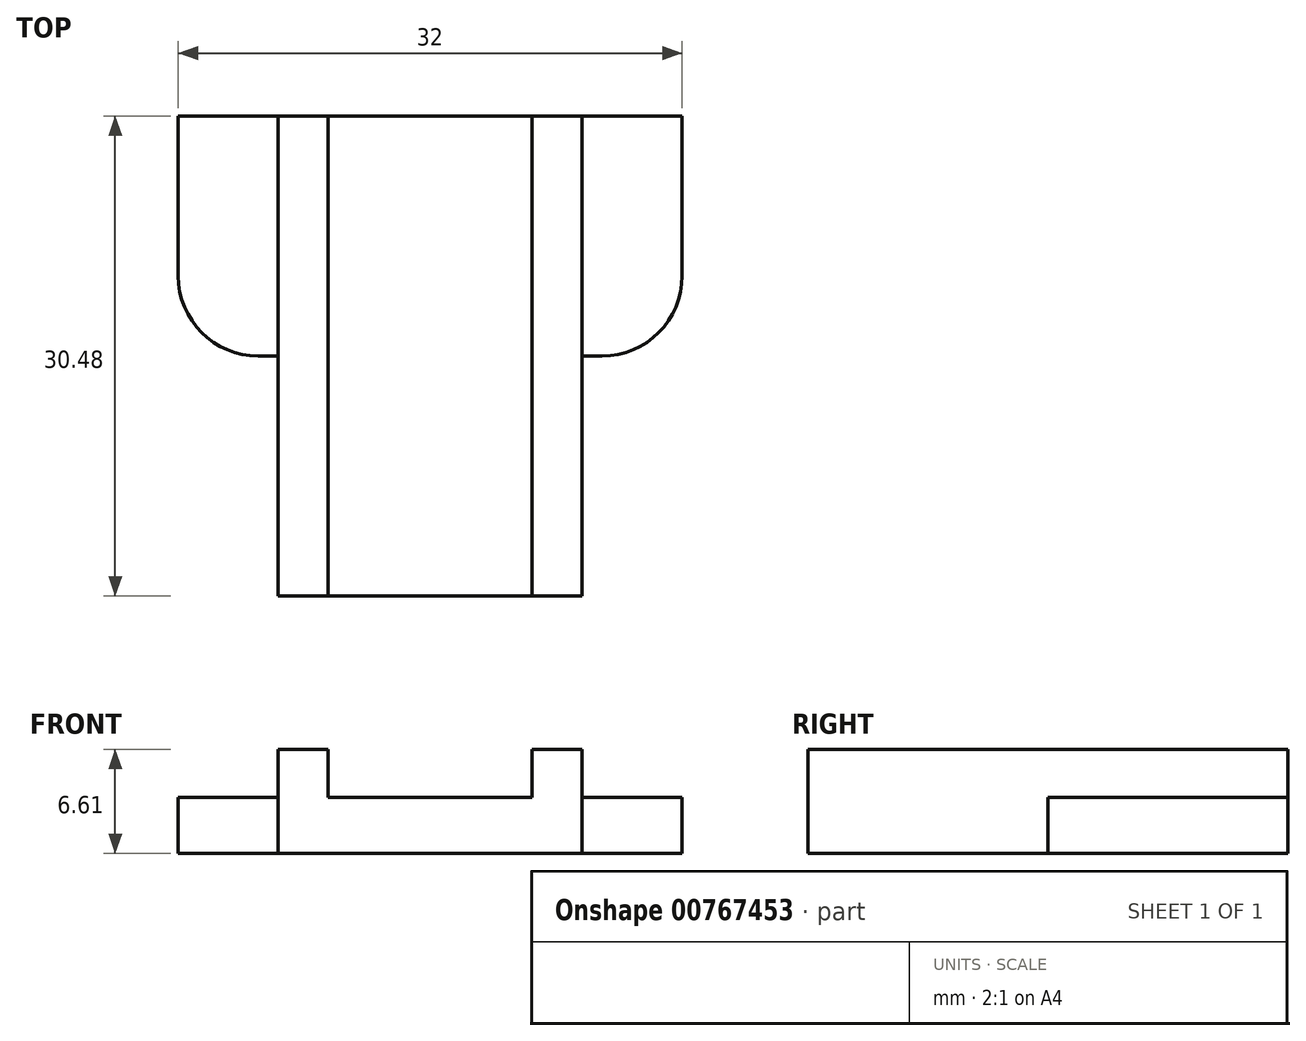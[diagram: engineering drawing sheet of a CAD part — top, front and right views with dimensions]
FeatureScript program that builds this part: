
annotation { "Feature Type Name" : "Feature", "Feature Type Description" : "" }
export const myFeature = defineFeature(function(context is Context, id is Id, definition is map)
    precondition{}
    {
        {
            var Q0;
            Q0=qCreatedBy(makeId("Front.planeOp"),FACE);
            var sketch = newSketch(context, id + "F0", { "sketchPlane" : qUnion([Q0])});
            skLineSegment(sketch, "E0.bottom", {"start": v(9.65, 1.78) * mm, "end": v(-9.65, 1.78) * mm});
            skLineSegment(sketch, "E0.top", {"start": v(9.65, -1.78) * mm, "end": v(-9.65, -1.78) * mm});
            skLineSegment(sketch, "E0.left", {"start": v(9.65, 1.78) * mm, "end": v(9.65, -1.78) * mm});
            skLineSegment(sketch, "E0.right", {"start": v(-9.65, 1.78) * mm, "end": v(-9.65, -1.78) * mm});
            skPoint(sketch, "E0.middle", {"position": v(0, 0) * mm});
            skLineSegment(sketch, "E1.bottom", {"start": v(9.65, 1.78) * mm, "end": v(6.48, 1.78) * mm});
            skLineSegment(sketch, "E1.top", {"start": v(9.65, 4.83) * mm, "end": v(6.48, 4.83) * mm});
            skLineSegment(sketch, "E1.left", {"start": v(9.65, 1.78) * mm, "end": v(9.65, 4.83) * mm});
            skLineSegment(sketch, "E1.right", {"start": v(6.48, 1.78) * mm, "end": v(6.48, 4.83) * mm});
            skPoint(sketch, "E1.middle", {"position": v(8.06, 3.3) * mm});
            skLineSegment(sketch, "E2.MirrorCS", {"start": v(-9.65, 1.78) * mm, "end": v(-6.48, 1.78) * mm});
            skLineSegment(sketch, "E3.MirrorCS", {"start": v(-6.48, 1.78) * mm, "end": v(-6.48, 4.83) * mm});
            skLineSegment(sketch, "E4.MirrorCS", {"start": v(-9.65, 4.83) * mm, "end": v(-6.48, 4.83) * mm});
            skLineSegment(sketch, "E5.MirrorCS", {"start": v(-9.65, 1.78) * mm, "end": v(-9.65, 4.83) * mm});
            skPoint(sketch, "E6.MirrorP", {"position": v(-8.06, 3.3) * mm});
            skLineSegment(sketch, "E7.bottom", {"start": v(6.48, 1.78) * mm, "end": v(-6.48, 1.78) * mm});
            skLineSegment(sketch, "E7.top", {"start": v(6.48, 4.83) * mm, "end": v(-6.48, 4.83) * mm});
            skLineSegment(sketch, "E8.bottom", {"start": v(9.65, 1.78) * mm, "end": v(16, 1.78) * mm});
            skLineSegment(sketch, "E8.top", {"start": v(9.65, -1.78) * mm, "end": v(16, -1.78) * mm});
            skLineSegment(sketch, "E8.right", {"start": v(16, 1.78) * mm, "end": v(16, -1.78) * mm});
            skLineSegment(sketch, "E9.MirrorCS", {"start": v(-9.65, -1.78) * mm, "end": v(-16, -1.78) * mm});
            skLineSegment(sketch, "E10.MirrorCS", {"start": v(-9.65, 1.78) * mm, "end": v(-16, 1.78) * mm});
            skLineSegment(sketch, "E11.MirrorCS", {"start": v(-16, 1.78) * mm, "end": v(-16, -1.78) * mm});
            skSolve(sketch);
        }
        {
            var Q0;
            Q0=makeQuery(id+"F0.imprint","IMPRINT",FACE,{"disambiguationData":[TD([[makeQuery(id+"F0.imprint","IMPRINT",EDGE,{"derivedFrom":sQuery(id+"F0.wireOp",EDGE,"E0.top")}),-1.0]])]});
            var Q1;
            Q1=makeQuery(id+"F0.imprint","IMPRINT",FACE,{"disambiguationData":[TD([[makeQuery(id+"F0.imprint","IMPRINT",EDGE,{"derivedFrom":sQuery(id+"F0.wireOp",EDGE,"E1.top")}),1.0]])]});
            var Q2;
            {var subQ2=sQuery(id+"F0.wireOp",EDGE,"E3.MirrorCS");Q2=makeQuery(id+"F0.imprint","IMPRINT",FACE,{"disambiguationData":[TD([[makeQuery(id+"F0.imprint","IMPRINT",EDGE,{"derivedFrom":subQ2}),1.0]])]});}
            extrude(context, id + "F1", {"entities" : qUnion([Q0, Q1, Q2]), "depth" : 30.48 * mm, "offsetDistance" : 25.4 * mm});
        }
        {
            var Q0;
            Q0=makeQuery(id+"F0.imprint","IMPRINT",FACE,{"disambiguationData":[TD([[makeQuery(id+"F0.imprint","IMPRINT",EDGE,{"derivedFrom":sQuery(id+"F0.wireOp",EDGE,"E0.left")}),1.0]])]});
            extrude(context, id + "F2", {"entities" : qUnion([Q0]), "operationType" : NewBodyOperationType.ADD, "depth" : 15.24 * mm, "offsetDistance" : 25.4 * mm});
        }
        {
            var Q0;
            Q0=makeQuery(id+"F0.imprint","IMPRINT",FACE,{"disambiguationData":[TD([[makeQuery(id+"F0.imprint","IMPRINT",EDGE,{"derivedFrom":sQuery(id+"F0.wireOp",EDGE,"E0.right")}),-1.0]])]});
            extrude(context, id + "F3", {"entities" : qUnion([Q0]), "operationType" : NewBodyOperationType.ADD, "depth" : 15.24 * mm, "offsetDistance" : 25.4 * mm});
        }
        {
            var Q0;
            Q0=makeQuery(id+"F3.opExtrude","CAP_EDGE",EDGE,{"disambiguationData":[OSD([sQuery(id+"F0.wireOp",EDGE,"E11.MirrorCS")])],"isStart":false});
            var Q1;
            Q1=makeQuery(id+"F2.opExtrude","CAP_EDGE",EDGE,{"disambiguationData":[OSD([sQuery(id+"F0.wireOp",EDGE,"E8.right")])],"isStart":false});
            fillet(context, id + "F4", {"entities" : qUnion([Q0, Q1]), "radius" : 5.08 * mm, "tangentPropagation" : true, "allowEdgeOverflow" : false});
        }
    });
